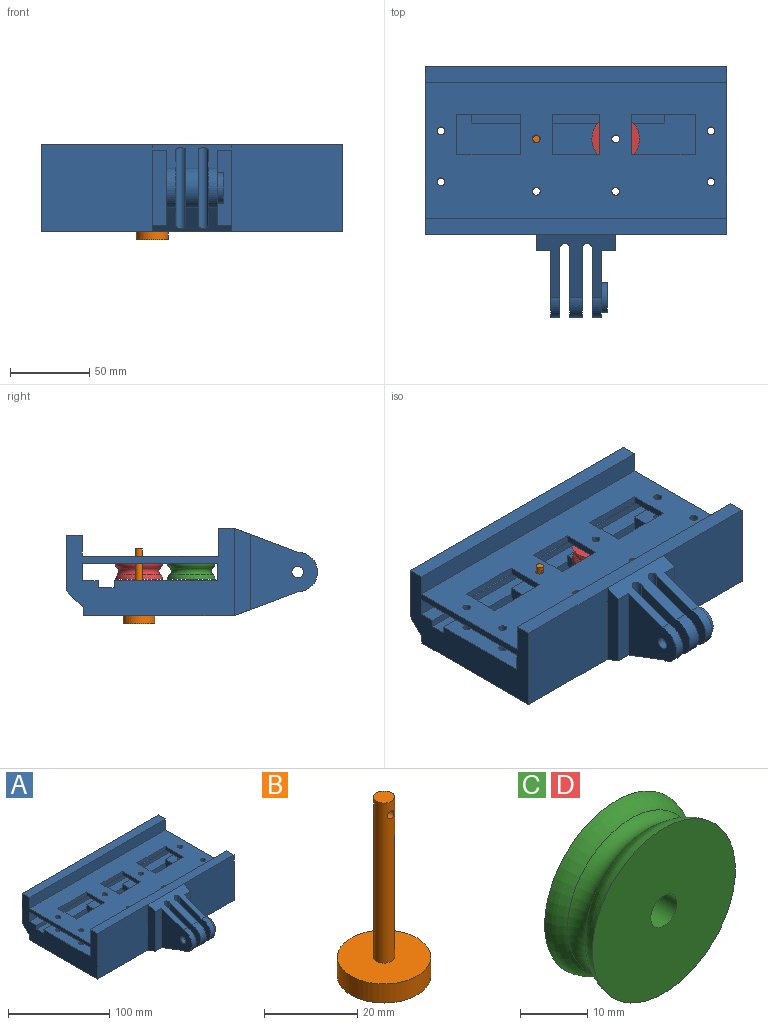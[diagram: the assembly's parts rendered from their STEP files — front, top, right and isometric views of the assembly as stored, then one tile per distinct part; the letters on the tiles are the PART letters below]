
ASSEMBLY  parts=4 mates=3
PART A: 98 faces, bbox 190x158.1x55 mm
  f0: plane 25.61x12mm, normal (1,0,0), area 291.6mm2, adj f4,f7,f24,f80,f92,f94
  f1: plane 25.61x12mm, normal (-1,0,0), area 291.6mm2, adj f4,f7,f23,f80,f92,f94
  f2: plane 25.61x12mm, normal (1,0,0), area 291.6mm2, adj f5,f8,f23,f80,f92,f94
  f3: plane 25.61x12mm, normal (-1,0,0), area 291.6mm2, adj f6,f11,f24,f80,f92,f94
  f4: plane 30x20mm, normal (0,0,1), area 600mm2, adj f0,f1,f7,f94
  f5: plane 40x25.61mm, normal (0,0,1), area 908.8mm2, adj f2,f8,f9,f80,f94,f97
  f6: plane 40x25.61mm, normal (0,0,1), area 853.3mm2, adj f3,f10,f11,f80,f94,f96
  f7: plane 30x12mm, normal (0,1,0), area 360mm2, adj f0,f1,f4,f92
  f8: plane 40x12mm, normal (0,1,0), area 480mm2, adj f2,f5,f9,f92
  f9: plane 25.61x12mm, normal (-1,0,0), area 307.3mm2, adj f5,f8,f67,f80,f92
  f10: plane 25.61x12mm, normal (1,0,0), area 307.3mm2, adj f6,f11,f22,f80,f92
  f11: plane 40x12mm, normal (0,1,0), area 480mm2, adj f3,f6,f10,f92
  f12: cylinder r=2.5mm len=22mm, axis (0,0,-1), area 345.6mm2, adj f20,f92
  f13: cylinder r=2.5mm len=22mm, axis (0,0,-1), area 345.6mm2, adj f20,f92
  f14: cylinder r=2.5mm len=22mm, axis (0,0,-1), area 345.6mm2, adj f20,f92
  f15: cylinder r=2.5mm len=22mm, axis (0,0,-1), area 345.6mm2, adj f20,f92
  f16: cylinder r=2.5mm len=22mm, axis (0,0,-1), area 345.6mm2, adj f20,f92
  f17: cylinder r=2.5mm len=22mm, axis (0,0,-1), area 345.6mm2, adj f20,f92
  f18: cylinder r=2.5mm len=22mm, axis (0,0,-1), area 345.6mm2, adj f20,f92
  f19: cylinder r=2.5mm len=22mm, axis (0,0,-1), area 345.6mm2, adj f20,f92
  f20: plane 190x95mm, normal (0,0,-1), area 17892.9mm2, adj f12,f13,f14,f15,f16,f17,f18,f19
  f21: plane 190x85.61mm, normal (0,0,1), area 13291.4mm2, adj f25,f33,f35,f39,f68,f69,f70,f71
  f22: plane 20x4.5mm, normal (0,1,0), area 90mm2, adj f10,f35,f66,f92
  f23: plane 20x4.5mm, normal (0,1,0), area 90mm2, adj f1,f2,f66,f92
  f24: plane 20x4.5mm, normal (0,1,0), area 90mm2, adj f0,f3,f66,f92
  f25: plane 190x13.11mm, normal (0,-1,0), area 2490.3mm2, adj f21,f33,f35,f38
  f26: plane 19.05x19.05mm, normal (1,0,0), area 176.9mm2, adj f54,f55,f56,f57,f58,f59,f60
  f27: plane 50x40mm, normal (0,-0.35,-0.94), area 1095.4mm2, adj f20,f29,f30,f31,f42,f43,f44,f45
  f28: plane 50x40mm, normal (0,-0.35,0.94), area 1095.4mm2, adj f29,f30,f31,f41,f42,f43,f44,f45
  f29: cylinder r=12.5mm len=25mm, axis (-1,0,0), area 224.4mm2, adj f27,f28,f44,f52
  f30: cylinder r=12.5mm len=25mm, axis (-1,0,0), area 299.2mm2, adj f27,f28,f49,f53
  f31: plane 55x10mm, normal (1,0,0), area 512.5mm2, adj f27,f28,f40,f47
  f32: plane 70x55mm, normal (0,-1,0), area 3850mm2, adj f20,f35,f41,f43
  f33: plane 105.61x55mm, normal (1,0,0), area 3177mm2, adj f20,f21,f25,f34,f36,f37,f38,f39
  f34: plane 190x5mm, normal (0,1,0), area 950mm2, adj f20,f33,f35,f36
  f35: plane 105.61x55mm, normal (-1,0,0), area 3177mm2, adj f20,f21,f22,f25,f32,f34,f36,f37
  f36: plane 190x10.61mm, normal (0,0.71,-0.71), area 2850mm2, adj f33,f34,f35,f37
  f37: plane 190x35mm, normal (0,1,0), area 6650mm2, adj f33,f35,f36,f38
  f38: plane 190x10mm, normal (0,0,1), area 1900mm2, adj f25,f33,f35,f37
  f39: plane 190x17.5mm, normal (0,1,0), area 3325mm2, adj f21,f33,f35,f41
  f40: plane 70x55mm, normal (0,-1,0), area 3850mm2, adj f20,f31,f33,f41
  f41: plane 190x10mm, normal (0,0,1), area 1900mm2, adj f28,f32,f33,f35,f39,f40
  f42: cylinder r=12.5mm len=25mm, axis (-1,0,0), area 224.4mm2, adj f27,f28,f46,f50
  f43: plane 55x10mm, normal (-1,0,0), area 512.5mm2, adj f27,f28,f32,f45
  f44: plane 47.5x42.5mm, normal (-1,0,0), area 1291.1mm2, adj f27,f28,f29,f45,f64
  f45: plane 47.5x9.13mm, normal (0,-1,0), area 433.4mm2, adj f27,f28,f43,f44
  f46: plane 47.5x42.5mm, normal (1,0,0), area 1047.9mm2, adj f27,f28,f42,f47,f54
  f47: plane 47.5x9.13mm, normal (0,-1,0), area 433.4mm2, adj f27,f28,f31,f46
  f48: cylinder r=3.17mm len=50.73mm, axis (0,0,-1), area 497.3mm2, adj f27,f28,f49,f50
  f49: plane 48.34x43.62mm, normal (1,0,0), area 1344.5mm2, adj f27,f28,f30,f48,f63
  f50: plane 48.34x43.62mm, normal (-1,0,0), area 1344.5mm2, adj f27,f28,f42,f48,f62
  f51: cylinder r=3.17mm len=50.73mm, axis (0,0,-1), area 497.3mm2, adj f27,f28,f52,f53
  f52: plane 48.34x43.62mm, normal (1,0,0), area 1344.5mm2, adj f27,f28,f29,f51,f64
  f53: plane 48.34x43.62mm, normal (-1,0,0), area 1344.5mm2, adj f27,f28,f30,f51,f63
  f54: cylinder r=9.53mm len=19.05mm, axis (-1,0,0), area 232.7mm2, adj f26,f46
  f55: plane 5.59x4.84mm, normal (0,0.87,0.5), area 31.2mm2, adj f26,f56,f60,f61
  f56: plane 6.45x4.84mm, normal (0,0,1), area 31.2mm2, adj f26,f55,f57,f61
  f57: plane 5.59x4.84mm, normal (0,-0.87,0.5), area 31.2mm2, adj f26,f56,f58,f61
  f58: plane 5.59x4.84mm, normal (0,-0.87,-0.5), area 31.2mm2, adj f26,f57,f59,f61
  f59: plane 6.45x4.84mm, normal (0,0,-1), area 31.2mm2, adj f26,f58,f60,f61
  f60: plane 5.59x4.84mm, normal (0,0.87,-0.5), area 31.2mm2, adj f26,f55,f59,f61
  f61: plane 12.91x11.18mm, normal (1,0,0), area 66.3mm2, adj f55,f56,f57,f58,f59,f60,f62
  f62: cylinder r=3.65mm len=7.3mm, axis (1,0,0), area 109.2mm2, adj f50,f61
  f63: cylinder r=3.65mm len=7.62mm, axis (1,0,0), area 174.8mm2, adj f49,f53
  f64: cylinder r=3.65mm len=7.3mm, axis (1,0,0), area 131.1mm2, adj f44,f52
  f65: plane 190x4.5mm, normal (0,-1,0), area 855mm2, adj f33,f35,f66,f91
  f66: plane 190x10mm, normal (0,0,1), area 1900mm2, adj f22,f23,f24,f33,f35,f65,f67,f80
  f67: plane 20x4.5mm, normal (0,1,0), area 90mm2, adj f9,f33,f66,f92
  f68: plane 30x4.5mm, normal (0,-1,0), area 135mm2, adj f21,f69,f71,f93
  f69: plane 25.61x4.5mm, normal (1,0,0), area 115.2mm2, adj f21,f68,f70,f93
  f70: plane 30x4.5mm, normal (0,1,0), area 135mm2, adj f21,f69,f71,f93
  f71: plane 25.61x4.5mm, normal (-1,0,0), area 115.2mm2, adj f21,f68,f70,f93
  f72: plane 25.61x4.5mm, normal (1,0,0), area 115.2mm2, adj f21,f73,f75,f93
  f73: plane 40x4.5mm, normal (0,1,0), area 180mm2, adj f21,f72,f74,f93
  f74: plane 25.61x4.5mm, normal (-1,0,0), area 115.2mm2, adj f21,f73,f75,f93
  f75: plane 40x4.5mm, normal (0,-1,0), area 180mm2, adj f21,f72,f74,f93
  f76: plane 40x4.5mm, normal (0,-1,0), area 180mm2, adj f21,f77,f79,f93
  f77: plane 25.61x4.5mm, normal (1,0,0), area 115.2mm2, adj f21,f76,f78,f93
  f78: plane 40x4.5mm, normal (0,1,0), area 180mm2, adj f21,f77,f79,f93
  f79: plane 25.61x4.5mm, normal (-1,0,0), area 115.2mm2, adj f21,f76,f78,f93
  f80: plane 150x7.52mm, normal (0,-1,0), area 1051.5mm2, adj f0,f1,f2,f3,f5,f6,f9,f10
  f81: cylinder r=2.5mm len=5mm, axis (0,0,-1), area 70.7mm2, adj f21,f93
  f82: cylinder r=2.5mm len=5mm, axis (0,0,-1), area 70.7mm2, adj f21,f93
  f83: cylinder r=2.5mm len=5mm, axis (0,0,-1), area 70.7mm2, adj f21,f93
  f84: cylinder r=2.5mm len=5mm, axis (0,0,-1), area 70.7mm2, adj f21,f93
  f85: cylinder r=2.5mm len=5mm, axis (0,0,-1), area 70.7mm2, adj f21,f93
  f86: cylinder r=2.5mm len=5mm, axis (0,0,-1), area 70.7mm2, adj f21,f93
  f87: cylinder r=2.5mm len=5mm, axis (0,0,-1), area 70.7mm2, adj f21,f93
  f88: cylinder r=2.5mm len=5mm, axis (0,0,-1), area 70.7mm2, adj f21,f93
  f89: plane 190x11mm, normal (0,-1,0), area 2090mm2, adj f33,f35,f91,f93
  f90: plane 190x11mm, normal (0,1,0), area 2090mm2, adj f33,f35,f92,f93
  f91: plane 190x10mm, normal (0,0,1), area 1900mm2, adj f33,f35,f65,f89
  f92: plane 190x65mm, normal (0,0,1), area 9376.2mm2, adj f0,f1,f2,f3,f7,f8,f9,f10
  f93: plane 190x85mm, normal (0,0,-1), area 13176.2mm2, adj f33,f35,f68,f69,f70,f71,f72,f73
  f94: plane 121.1x5.63mm, normal (0,0.71,-0.71), area 320.3mm2, adj f0,f1,f2,f3,f4,f5,f6,f80
  f95: plane 121.1x5.63mm, normal (0,0,1), area 681.2mm2, adj f80,f94,f96,f97
  f96: plane 5.63x0.02mm, normal (1,0,0), area 0.1mm2, adj f6,f80,f94,f95
  f97: plane 5.63x0.02mm, normal (-1,0,0), area 0.1mm2, adj f5,f80,f94,f95
PART B: 6 faces, bbox 20x20x47 mm
  f0: cylinder r=10mm len=20mm, axis (0,0,-1), area 314.2mm2, adj f1,f2
  f1: plane 20x20mm, normal (0,0,1), area 298.3mm2, adj f0,f3
  f2: plane 20x20mm, normal (0,0,-1), area 314.2mm2, adj f0
  f3: cylinder r=2.25mm len=42mm, axis (0,0,-1), area 587.3mm2, adj f1,f4,f5
  f4: plane 4.5x4.5mm, normal (0,0,1), area 15.9mm2, adj f3
  f5: cylinder r=1mm len=4.5mm, axis (0,-1,0), area 26.8mm2, adj f3
PART C: 6 faces, bbox 32.6x11.3x32.6 mm
  f0: plane 30x30mm, normal (0,-1,0), area 683.1mm2, adj f3,f5
  f1: torus R=15mm, axis (0,-1,0), area 340.7mm2, adj f3,f4
  f2: plane 30x30mm, normal (0,1,0), area 683.1mm2, adj f4,f5
  f3: torus R=10.04mm, axis (0,1,0), area 326.1mm2, adj f0,f1
  f4: torus R=10.04mm, axis (0,-1,0), area 326.1mm2, adj f1,f2
  f5: cylinder r=2.75mm len=10mm, axis (0,-1,0), area 172.8mm2, adj f0,f2
PART D: same geometry as C
PLACE A t=(-59.03,18.85,16.73)mm
PLACE B t=(-84.03,28.85,11.73)mm
PLACE C rot(axis=(1,0,0),90deg) t=(-34.03,-4.15,44.73)mm
PLACE D rot(axis=(-1,0,0),90deg) t=(-34.03,28.85,44.73)mm
MATE fastened C.f5 <-> A.f16  axis (0,0,1) through (-34.03,-4.15,49.73)mm
MATE fastened B.f3 <-> A.f19  axis (0,0,-1) through (-84.03,28.85,16.73)mm
MATE fastened D.f3 <-> A.f12  axis (0,0,1) through (-34.03,28.85,49.73)mm
